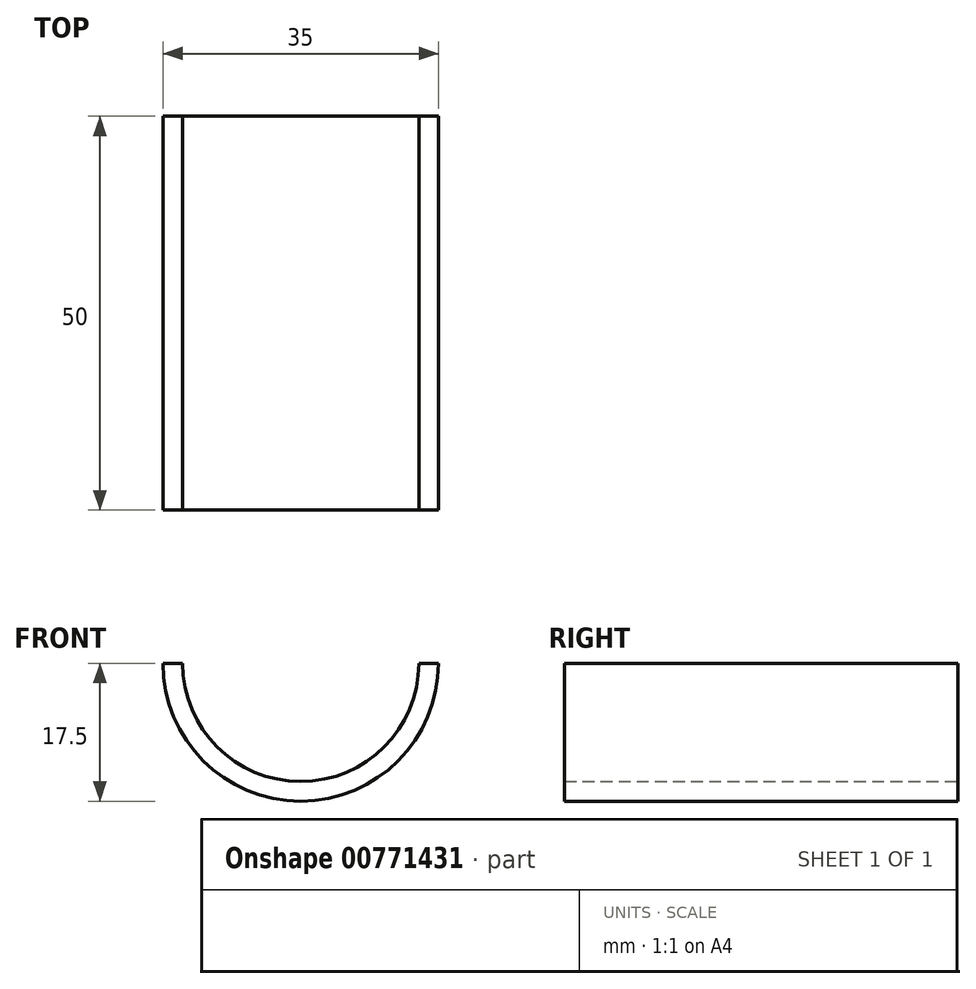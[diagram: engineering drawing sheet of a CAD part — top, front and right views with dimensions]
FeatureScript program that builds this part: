
annotation { "Feature Type Name" : "Feature", "Feature Type Description" : "" }
export const myFeature = defineFeature(function(context is Context, id is Id, definition is map)
    precondition{}
    {
        {
            var Q0;
            Q0=qCreatedBy(makeId("Front.planeOp"),FACE);
            var sketch = newSketch(context, id + "F0", { "sketchPlane" : qUnion([Q0])});
            skCircle(sketch, "E0", {"center": v(0, 0) * mm, "radius": 17.5 * mm});
            skCircle(sketch, "E1", {"center": v(0, 0) * mm, "radius": 15 * mm});
            skSolve(sketch);
        }
        {
            var Q0;
            Q0 = qSketchRegion(id + "F0", true);
            extrude(context, id + "F1", {"entities" : qUnion([Q0]), "endBound" : BoundingType.SYMMETRIC, "depth" : 50 * mm, "offsetDistance" : 25.4 * mm});
        }
        {
            var Q0;
            Q0=qCreatedBy(makeId("Front.planeOp"),FACE);
            var sketch = newSketch(context, id + "F2", { "sketchPlane" : qUnion([Q0])});
            skArc(sketch, "E2", {"start": v(12.92, 0) * mm, "mid": v(-0.32, 13.94) * mm, "end": v(-13.56, 0) * mm});
            skArc(sketch, "E3", {"start": v(19.62, 0) * mm, "mid": v(0.16, 20.13) * mm, "end": v(-19.3, 0) * mm});
            skLineSegment(sketch, "E4", {"start": v(-13.56, 0) * mm, "end": v(-19.3, 0) * mm});
            skLineSegment(sketch, "E5", {"start": v(12.92, 0) * mm, "end": v(19.62, 0) * mm});
            skSolve(sketch);
        }
        {
            var Q0;
            Q0 = qSketchRegion(id + "F2", true);
            extrude(context, id + "F3", {"entities" : qUnion([Q0]), "operationType" : NewBodyOperationType.REMOVE, "endBound" : BoundingType.SYMMETRIC, "oppositeDirection" : true, "depth" : 50 * mm, "offsetDistance" : 25.4 * mm});
        }
    });
